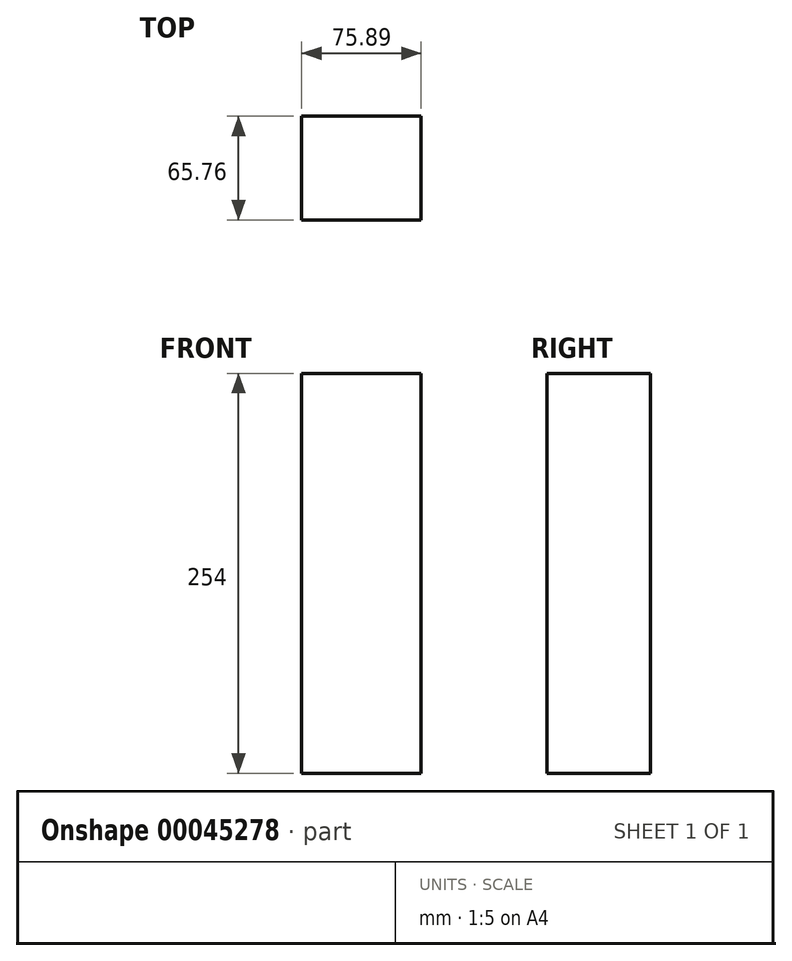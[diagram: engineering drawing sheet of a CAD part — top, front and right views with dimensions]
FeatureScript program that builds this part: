
annotation { "Feature Type Name" : "Feature", "Feature Type Description" : "" }
export const myFeature = defineFeature(function(context is Context, id is Id, definition is map)
    precondition{}
    {
        {
            var Q0;
            Q0=qCreatedBy(makeId("Top.planeOp"),FACE);
            var sketch = newSketch(context, id + "F0", { "sketchPlane" : qUnion([Q0])});
            skLineSegment(sketch, "E0.bottom", {"start": v(-47.5, -30.17) * mm, "end": v(28.38, -30.17) * mm});
            skLineSegment(sketch, "E0.top", {"start": v(-47.5, 35.59) * mm, "end": v(28.38, 35.59) * mm});
            skLineSegment(sketch, "E0.left", {"start": v(-47.5, -30.17) * mm, "end": v(-47.5, 35.59) * mm});
            skLineSegment(sketch, "E0.right", {"start": v(28.38, -30.17) * mm, "end": v(28.38, 35.59) * mm});
            skSolve(sketch);
        }
        {
            var Q0;
            Q0 = qSketchRegion(id + "F0", true);
            extrude(context, id + "F1", {"entities" : qUnion([Q0]), "depth" : 254 * mm});
        }
    });
